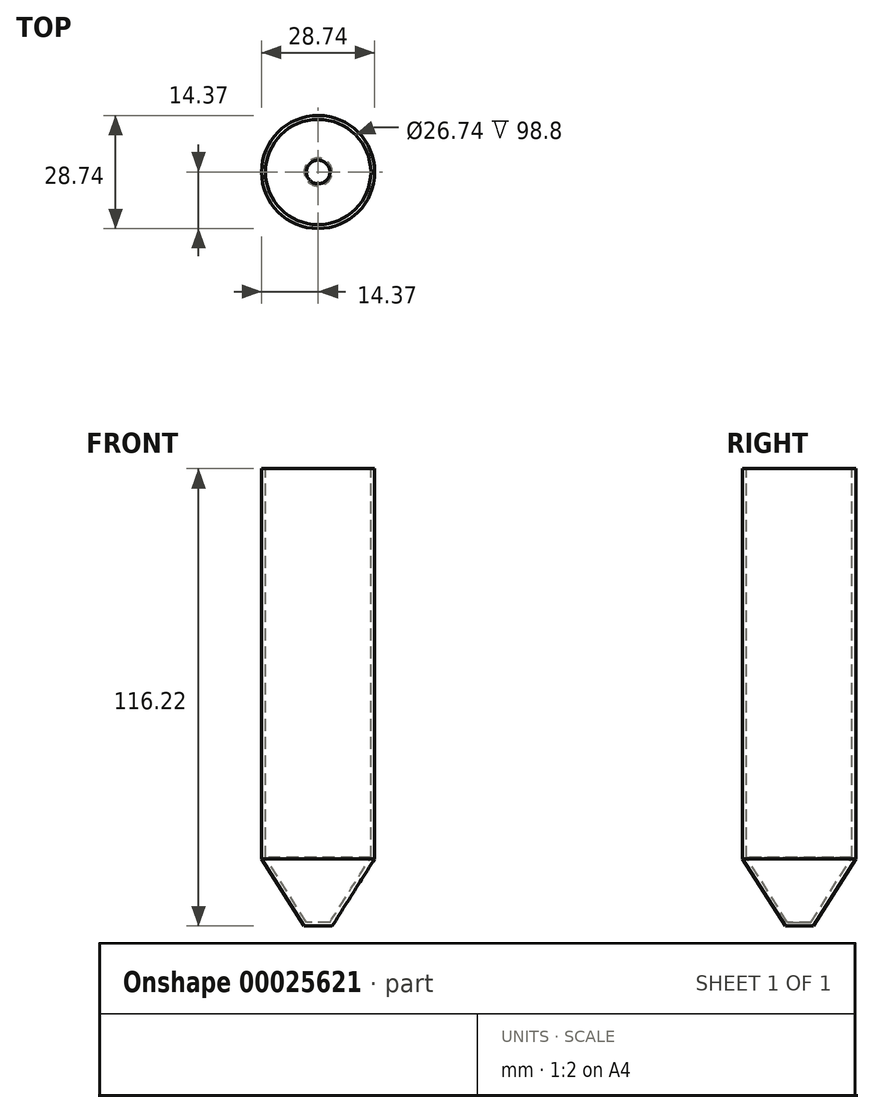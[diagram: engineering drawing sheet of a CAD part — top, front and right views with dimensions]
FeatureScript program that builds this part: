
annotation { "Feature Type Name" : "Feature", "Feature Type Description" : "" }
export const myFeature = defineFeature(function(context is Context, id is Id, definition is map)
    precondition{}
    {
        {
            var Q0;
            Q0=qCreatedBy(makeId("Front.planeOp"),FACE);
            var sketch = newSketch(context, id + "F0", { "sketchPlane" : qUnion([Q0])});
            skLineSegment(sketch, "E0", {"start": v(0, 0) * mm, "end": v(3, 0) * mm});
            skLineSegment(sketch, "E1", {"start": v(3, 0) * mm, "end": v(13.37, 16.42) * mm});
            skLineSegment(sketch, "E2", {"start": v(13.37, 16.42) * mm, "end": v(13.37, 115.22) * mm});
            skLineSegment(sketch, "E3.0", {"start": v(14.37, 16.13) * mm, "end": v(14.37, 115.22) * mm});
            skLineSegment(sketch, "E3.1", {"start": v(3.55, -1) * mm, "end": v(14.37, 16.13) * mm});
            skLineSegment(sketch, "E3.2", {"start": v(0, -1) * mm, "end": v(3.55, -1) * mm});
            skLineSegment(sketch, "E4", {"start": v(13.37, 115.22) * mm, "end": v(14.37, 115.22) * mm});
            skLineSegment(sketch, "E5", {"start": v(0, 0) * mm, "end": v(0, -1) * mm});
            skSolve(sketch);
        }
        {
            var Q0;
            Q0 = qSketchRegion(id + "F0", true);
            var Q1;
            Q1=sQuery(id+"F0.wireOp",EDGE,"E5");
            revolve(context, id + "F1", {"entities" : qUnion([Q0]), "axis" : qUnion([Q1]), "revolveType" : RevolveType.FULL});
        }
    });
